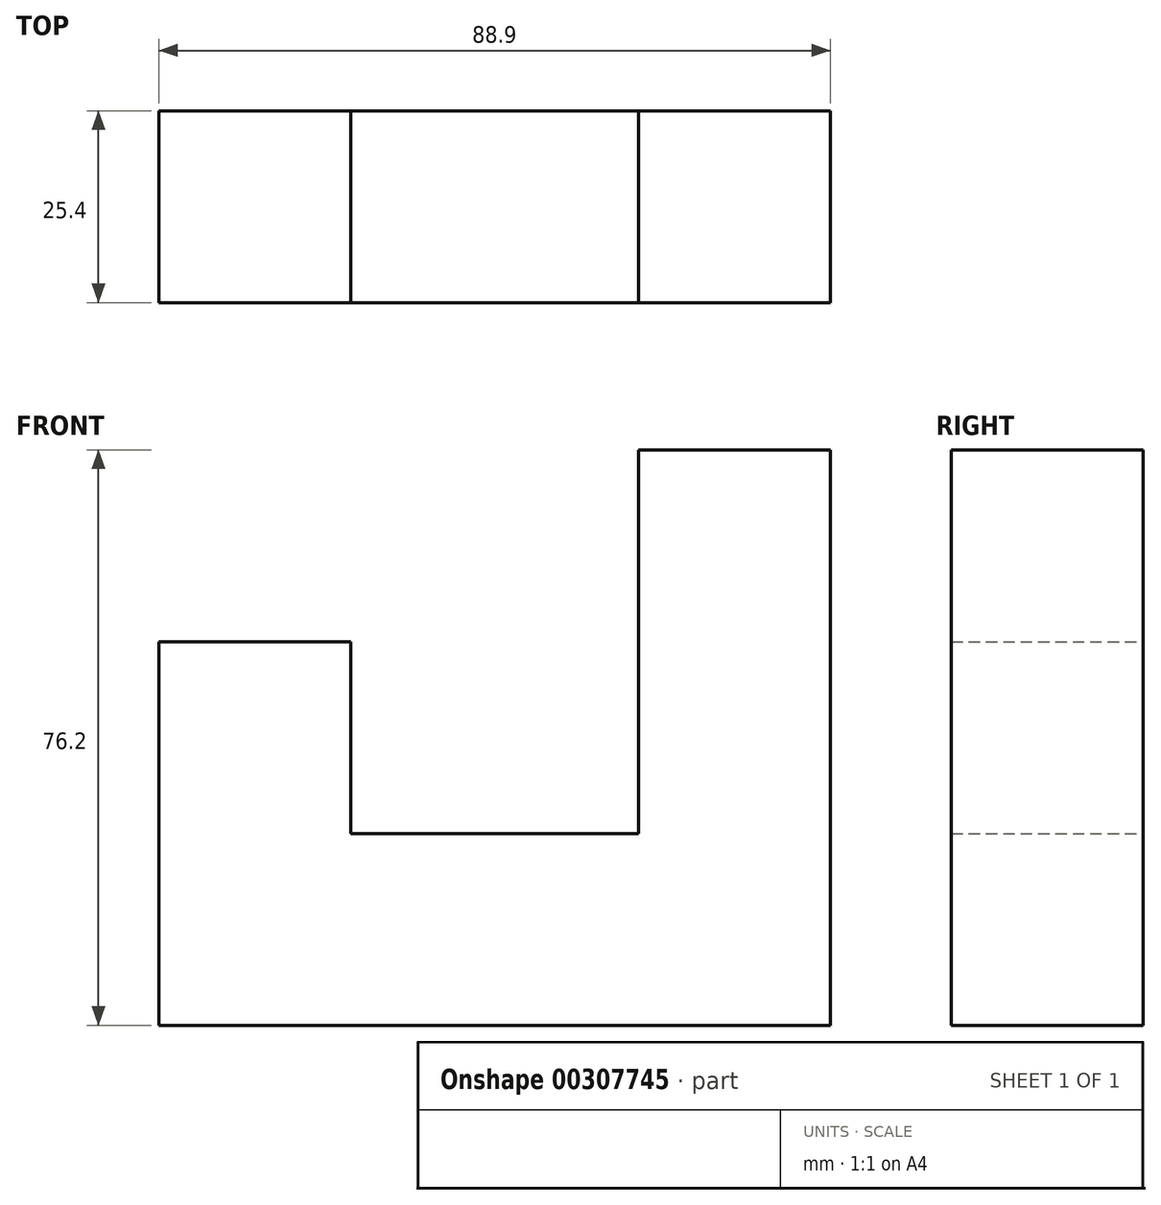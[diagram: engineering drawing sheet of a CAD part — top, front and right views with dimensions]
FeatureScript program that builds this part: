
annotation { "Feature Type Name" : "Feature", "Feature Type Description" : "" }
export const myFeature = defineFeature(function(context is Context, id is Id, definition is map)
    precondition{}
    {
        {
            var Q0;
            Q0=qCreatedBy(makeId("Front.planeOp"),FACE);
            var sketch = newSketch(context, id + "F0", { "sketchPlane" : qUnion([Q0])});
            skLineSegment(sketch, "E0", {"start": v(-40.37, -50.8) * mm, "end": v(48.53, -50.8) * mm});
            skLineSegment(sketch, "E1", {"start": v(48.53, -50.8) * mm, "end": v(48.53, 25.4) * mm});
            skLineSegment(sketch, "E2", {"start": v(48.53, 25.4) * mm, "end": v(23.13, 25.4) * mm});
            skLineSegment(sketch, "E3", {"start": v(23.13, 25.4) * mm, "end": v(23.13, -25.4) * mm});
            skLineSegment(sketch, "E4", {"start": v(23.13, -25.4) * mm, "end": v(-14.97, -25.4) * mm});
            skLineSegment(sketch, "E5", {"start": v(-14.97, -25.4) * mm, "end": v(-14.97, 0) * mm});
            skLineSegment(sketch, "E6", {"start": v(-40.37, -50.8) * mm, "end": v(-40.37, 0) * mm});
            skLineSegment(sketch, "E7", {"start": v(-40.37, 0) * mm, "end": v(-14.97, 0) * mm});
            skSolve(sketch);
        }
        {
            var Q0;
            Q0=makeQuery(id+"F0.imprint","IMPRINT",FACE,{"disambiguationData":[TD([[makeQuery(id+"F0.imprint","IMPRINT",EDGE,{"derivedFrom":sQuery(id+"F0.wireOp",EDGE,"E0")}),1.0]])]});
            extrude(context, id + "F1", {"entities" : qUnion([Q0]), "depth" : 25.4 * mm});
        }
    });
